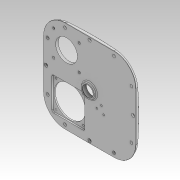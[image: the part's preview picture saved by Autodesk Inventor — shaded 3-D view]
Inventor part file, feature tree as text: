
AUTODESK INVENTOR PART (.ipt)
format: ipt  version: 2020 (Build 240168000, 168)  size: 944,640 bytes
history: native  units: mm
features: sketch x24, extrude x21, projected_geometry x6, other x4, plane x3, revolve x2, loft x1, fillet x1, chamfer x1
ambient origin geometry x8: Origin, YZ Plane, XZ Plane, XY Plane, X Axis, Y Axis, Z Axis, Center Point
bodies: Solid1 (feature_tree)
feature tree (63):
  other  "Blocks"
  sketch  "Sketch1"  dims[d1=170.0mm d2=170.0mm]
  extrude  "Extrusion1"  Depth=170.0mm
  extrude  "Extrusion2"  Depth=60.0mm TaperAngle=0.0deg
  plane  "Work Plane1"
  loft  "Loft1"
  extrude  "Extrusion3"  Depth=7.5mm
  plane  "Work Plane2"
  sketch  "Sketch6"  dims[d14=17.5mm d15=7.5mm]
  plane  "Work Plane3"
  sketch  "Sketch7"  dims[d16=10.0mm d17=65.0mm]
  extrude  "Extrusion4"  Depth=7.5mm
  extrude  "Extrusion5"  Depth=7.5mm
  extrude  "Extrusion9"  Depth=65.0mm
  sketch  "Sketch13"  dims[d23=0.0mm d24=90.0deg d25=5.0mm d26=0.0mm]
  extrude  "Extrusion10"  Depth=7.5mm
  extrude  "Extrusion11"  TaperAngle=0.0deg  [1 undecoded]
  extrude  "Extrusion12"  Depth=5.0mm TaperAngle=0.0deg
  revolve  "Revolution1"  [1 undecoded]
  extrude  "Extrusion13"  Depth=4.0mm
  extrude  "Extrusion14"  Depth=145.0mm
  extrude  "Extrusion15"  Depth=60.0mm TaperAngle=0.0deg
  revolve  "Revolution2"  [1 undecoded]
  fillet  "Fillet1"  Radius=47.0mm
  extrude  "Extrusion19"  Depth=60.0mm
  extrude  "Extrusion20"  Depth=42.426407mm
  extrude  "Extrusion22"  Depth=40.0mm
  extrude  "Extrusion23"  Depth=22.1mm
  extrude  "Extrusion24"  Depth=6.0mm TaperAngle=0.0deg
  extrude  "Extrusion25"  Depth=47.7mm
  extrude  "Extrusion17"  Depth=3.0mm
  extrude  "Extrusion18"  Depth=8.2mm
  extrude  "Extrusion26"  Depth=1.0mm
  chamfer  "Chamfer1"  Angle=90.0deg  [1 undecoded]
  sketch  "Sketch2"  dims[d3=40.0mm d4=60.0mm d5=0.0mm]
  other  "Block1"
  sketch  "Sketch3"  dims[d7=0.0mm d8=0.0mm d9=5.5mm]
  sketch  "Sketch4"  dims[d10=57.5mm d11=7.5mm]
  projected_geometry  "Projected Loop1"
  sketch  "Sketch5"  dims[d12=7.5mm d13=7.5mm]
  projected_geometry  "Projected Loop2"
  projected_geometry  "Projected Loop3"
  projected_geometry  "Projected Loop4"
  sketch  "Sketch8"  dims[d18=7.5mm d19=7.5mm]
  sketch  "Sketch12"  dims[d20=25.0mm d21=0.0mm d22=90.0deg]
  projected_geometry  "Projected Loop5"
  sketch  "Sketch14"  dims[d27=180.0mm d28=-3.0mm]
  sketch  "Sketch15"  dims[d29=2.5mm d30=4.0mm]
  sketch  "Sketch16"  dims[d31=10.0mm d32=0.0mm d33=145.0mm]
  sketch  "Sketch17"  dims[d34=48.25mm d35=0.0mm d54=60.0mm d55=0.0mm]
  sketch  "Sketch18"  dims[d56=5.0mm d57=0.0mm d58=47.0mm d59=47.0mm]
  sketch  "Sketch21"  dims[d60=60.0mm d61=60.0mm]
  sketch  "Sketch22"  dims[d62=42.426407mm d63=42.426407mm]
  sketch  "Sketch23"  dims[d64=4.4mm d65=40.0mm]
  sketch  "Sketch24"  dims[d66=6.0mm d67=0.0mm d68=22.1mm]
  sketch  "Sketch26"  dims[d69=16.0mm d70=6.0mm d71=0.0mm]
  sketch  "Sketch27"  dims[d72=35.0mm d73=47.7mm]
  sketch  "Sketch28"  dims[d74=25.0mm d75=3.0mm]
  sketch  "Sketch29"  dims[d77=7.2mm d78=8.2mm]
  sketch  "Sketch30"  dims[d79=0.5mm d80=1.0mm d81=90.0deg d82=60.0mm d83=10.0mm d85=5.5mm d86=9.0mm d87=40.0mm d89=360.0deg d91=48.25mm d92=0.0mm d93=9.5mm d94=40.0mm d96=360.0deg d98=16.0mm d99=0.0mm d100=0.0mm d101=0.0mm d106=12.0mm d107=12.0mm d109=3.3mm d110=0.0mm d111=0.0mm d112=7.0mm d113=135.0deg d114=0.5mm d115=1.0mm d116=2.0mm d117=19.198622mm d118=90.0deg d119=2.0mm d120=5.8mm d121=2.5mm d122=0.0mm d124=10.0mm d125=0.0mm d126=60.0mm d127=60.0mm d128=50.0mm d129=58.0mm d130=3.3mm d133=0.0mm d134=0.0mm d139=39.0mm d140=39.0mm d141=60.5mm d142=11.25mm d143=0.0mm d144=80.0mm d145=3.5mm d146=40.0mm d148=360.0deg d150=0.0mm d151=0.0mm d152=6.0mm d153=3.0mm d154=0.0mm d155=7.3mm d156=2.0mm d157=0.0mm d158=25.0mm d159=45.0deg d160=1.5mm d161=0.0mm d162=32.0mm d163=0.5mm d164=2.0mm d165=45.0deg d166=2.5mm d167=0.0mm d168=3.0mm]
  projected_geometry  "Projected Loop6"
  other  "Block1:1"
  other  "Block1:2"
note: 4 required parameter values undecoded (feature->parameter linkage not recoverable at this tier; creation-order binding heuristic only, values carry confidence <= 0.55)